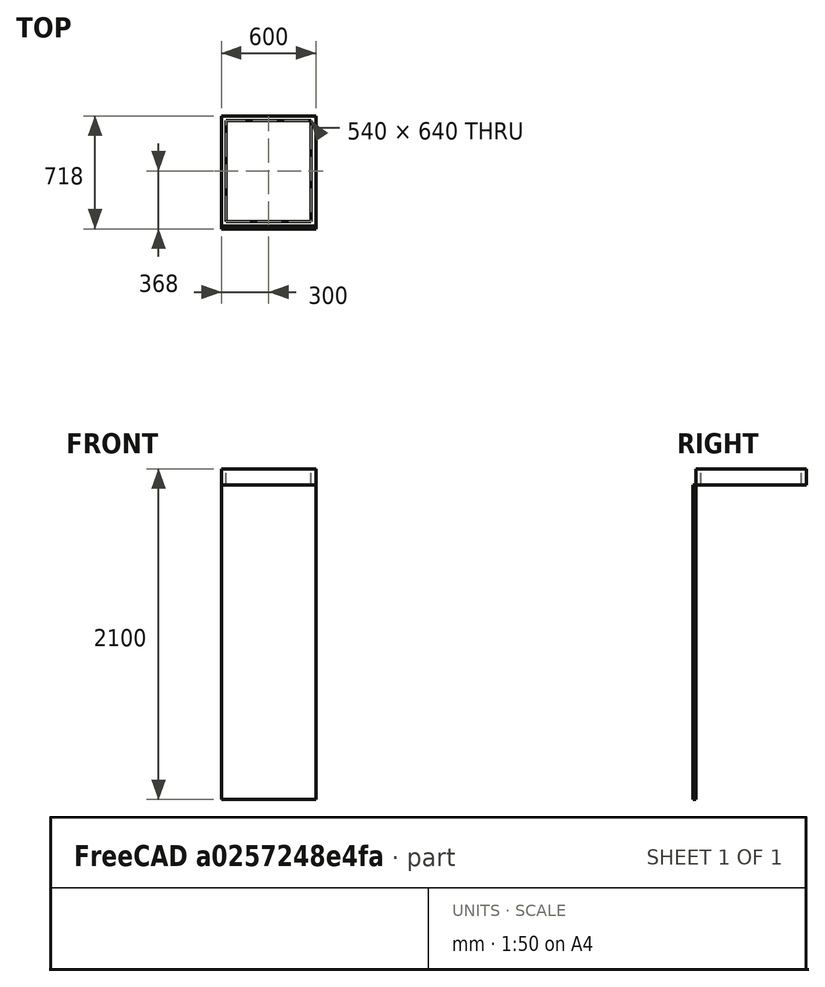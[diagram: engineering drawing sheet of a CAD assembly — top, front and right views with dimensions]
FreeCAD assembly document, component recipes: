
FREECAD ASSEMBLY — COMPONENT RECIPES ("mesa")

This assembly document has 2 components, labeled P0..P1 below (a component is one placed body or linked part). 2 of them carry a construction recipe — the FreeCAD feature program that regenerates the part from scratch, quoted from this document or its linked companion documents; the rest are supplied as boundary geometry only. No exploded tour is included for this assembly.
COMPONENT P0 — recipe-attached ("patas mesa001", modeled in this document).
Construction recipe (the document's own serialized feature program — sketch geometry with constraints, then the solid features built on it; lengths are millimeters unless a unit is written):

FEATURE [Sketcher::SketchObject] Sketch
  AttachmentSupport = -> [XY_Plane]
  FullyConstrained = true
  MapMode = 5
  sketch-geometry (8):
    g0: LineSegment StartX=0 StartY=0 StartZ=0 EndX=600 EndY=0 EndZ=0
    g1: LineSegment StartX=600 StartY=0 StartZ=0 EndX=600 EndY=700 EndZ=0
    g2: LineSegment StartX=600 StartY=700 StartZ=0 EndX=0 EndY=700 EndZ=0
    g3: LineSegment StartX=0 StartY=700 StartZ=0 EndX=0 EndY=0 EndZ=0
    g4: LineSegment StartX=30 StartY=670 StartZ=0 EndX=30 EndY=30 EndZ=0
    g5: LineSegment StartX=30 StartY=30 StartZ=0 EndX=570 EndY=30 EndZ=0
    g6: LineSegment StartX=570 StartY=30 StartZ=0 EndX=570 EndY=670 EndZ=0
    g7: LineSegment StartX=570 StartY=670 StartZ=0 EndX=30 EndY=670 EndZ=0
  constraints (23):
    c: Coincident(g0,g1)
    c: Coincident(g1,g2)
    c: Coincident(g2,g3)
    c: Coincident(g3,g0)
    c: Horizontal(g0)
    c: Horizontal(g2)
    c: Vertical(g1)
    c: Vertical(g3)
    c: Distance(g1,g3) = 600
    c: Distance(g0,g2) = 700
    c: Coincident(g0,g-1)
    c: Coincident(g4,g5)
    c: Coincident(g5,g6)
    c: Coincident(g6,g7)
    c: Coincident(g7,g4)
    c: Vertical(g4)
    c: Vertical(g6)
    c: Horizontal(g5)
    c: Horizontal(g7)
    c: Distance(g4,g3) = 30
    c: Distance(g1,g6) = 30
    c: Distance(g7,g2) = 30
    c: Distance(g0,g5) = 30
FEATURE [PartDesign::Pad] Pad
  Direction = (0,0,1)
  Length = 100
  Length2 = 10
  Profile = -> Sketch
  ReferenceAxis = -> Sketch [N_Axis]
  Refine = true
  Suppressed = false
  Type = 0
FEATURE [PartDesign::Body] Body  label="patas mesa"
  AllowCompound = false
  Group = -> [Sketch,Pad]
  Origin = -> Origin
  Tip = -> Pad
COMPONENT P1 — same part as P0; its construction recipe is shown at P0.
PROVENANCE & LICENSES
A FreeCAD (.FCStd) document from a public repository crawl; recipes are the document's own serialized feature recipes (and, for linked parts, companion documents' recipes).
License: as declared in the source repository (recorded in the dataset sidecar).
